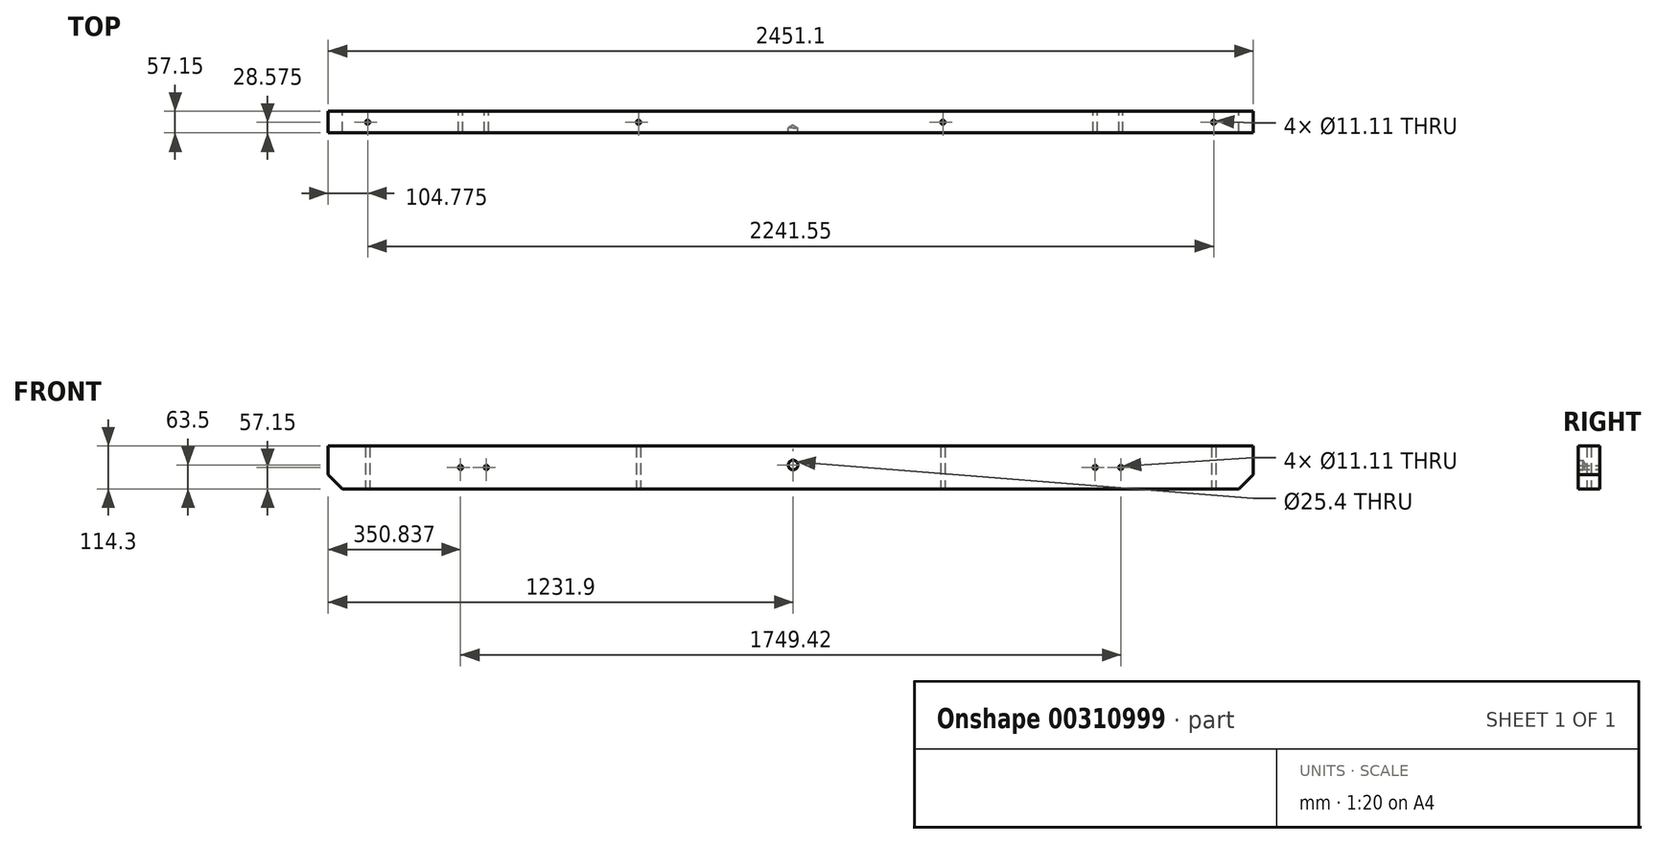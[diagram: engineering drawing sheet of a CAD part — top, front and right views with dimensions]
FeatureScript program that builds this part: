
annotation { "Feature Type Name" : "Feature", "Feature Type Description" : "" }
export const myFeature = defineFeature(function(context is Context, id is Id, definition is map)
    precondition{}
    {
        {
            var Q0;
            Q0=qCreatedBy(makeId("Front.planeOp"),FACE);
            var sketch = newSketch(context, id + "F0", { "sketchPlane" : qUnion([Q0])});
            skLineSegment(sketch, "E0", {"start": v(0, 0) * mm, "end": v(2451.1, 0) * mm});
            skLineSegment(sketch, "E1", {"start": v(2451.1, 0) * mm, "end": v(2451.1, -76.2) * mm});
            skLineSegment(sketch, "E2", {"start": v(0, 0) * mm, "end": v(0, -76.2) * mm});
            skLineSegment(sketch, "E3", {"start": v(0, -76.2) * mm, "end": v(38.1, -114.3) * mm});
            skLineSegment(sketch, "E4", {"start": v(2413, -114.3) * mm, "end": v(2451.1, -76.2) * mm});
            skLineSegment(sketch, "E5", {"start": v(38.1, -114.3) * mm, "end": v(2413, -114.3) * mm});
            skSolve(sketch);
        }
        {
            var Q0;
            Q0=makeQuery(id+"F0.imprint","IMPRINT",FACE,{"disambiguationData":[TD([[makeQuery(id+"F0.imprint","IMPRINT",EDGE,{"derivedFrom":sQuery(id+"F0.wireOp",EDGE,"E0")}),-1.0]])]});
            extrude(context, id + "F1", {"entities" : qUnion([Q0]), "depth" : 57.15 * mm});
        }
        {
            var Q0;
            Q0=makeQuery(id+"F1.opExtrude","SWEPT_FACE",FACE,{"disambiguationData":[OSD([sQuery(id+"F0.wireOp",EDGE,"E0")])]});
            var sketch = newSketch(context, id + "F2", { "sketchPlane" : qUnion([Q0])});
            skLineSegment(sketch, "E6", {"start": v(2451.1, -28.57) * mm, "end": v(0, -28.58) * mm, "construction": true});
            skLineSegment(sketch, "E7", {"start": v(104.78, 0) * mm, "end": v(104.78, -57.15) * mm, "construction": true});
            skLineSegment(sketch, "E8", {"start": v(822.33, 0) * mm, "end": v(822.33, -57.15) * mm, "construction": true});
            skLineSegment(sketch, "E9", {"start": v(2346.33, 0) * mm, "end": v(2346.33, -57.15) * mm, "construction": true});
            skLineSegment(sketch, "E10", {"start": v(1628.78, 0) * mm, "end": v(1628.78, -57.15) * mm, "construction": true});
            skPoint(sketch, "E11", {"position": v(2346.33, -28.57) * mm});
            skPoint(sketch, "E12", {"position": v(1628.78, -28.57) * mm});
            skPoint(sketch, "E13", {"position": v(822.33, -28.58) * mm});
            skPoint(sketch, "E14", {"position": v(104.78, -28.58) * mm});
            skSolve(sketch);
        }
        {
            var Q0;
            Q0=sQuery(id+"F2.wireOp",VERTEX,"E14");
            var Q1;
            Q1=sQuery(id+"F2.wireOp",VERTEX,"E13");
            var Q2;
            Q2=sQuery(id+"F2.wireOp",VERTEX,"E12");
            var Q3;
            Q3=sQuery(id+"F2.wireOp",VERTEX,"E11");
            var Q4;
            Q4=makeQuery(id+"F1.opExtrude","SWEPT_BODY",BODY,{"disambiguationData":[OSD([sQuery(id+"F0.wireOp",EDGE,"E0"),sQuery(id+"F0.wireOp",EDGE,"E1"),sQuery(id+"F0.wireOp",EDGE,"E2"),sQuery(id+"F0.wireOp",EDGE,"E3"),sQuery(id+"F0.wireOp",EDGE,"E4"),sQuery(id+"F0.wireOp",EDGE,"E5")])]});
            hole(context, id + "F3", {"style" : HoleStyle.SIMPLE, "endStyle" : HoleEndStyle.THROUGH, "holeDiameter" : 11.1 * mm, "tappedDepth" : 12.7 * mm, "tapClearance" : 3, "locations" : qUnion([Q0, Q1, Q2, Q3]), "scope" : qUnion([Q4])});
        }
        {
            var Q0;
            Q0=makeQuery(id+"F1.opExtrude","CAP_FACE",FACE,{"disambiguationData":[OSD([sQuery(id+"F0.wireOp",EDGE,"E0"),sQuery(id+"F0.wireOp",EDGE,"E1"),sQuery(id+"F0.wireOp",EDGE,"E2"),sQuery(id+"F0.wireOp",EDGE,"E3"),sQuery(id+"F0.wireOp",EDGE,"E4"),sQuery(id+"F0.wireOp",EDGE,"E5")])],"isStart":false});
            var sketch = newSketch(context, id + "F4", { "sketchPlane" : qUnion([Q0])});
            skLineSegment(sketch, "E15", {"start": v(0, -57.15) * mm, "end": v(2451.1, -57.15) * mm, "construction": true});
            skPoint(sketch, "E16", {"position": v(350.84, -57.15) * mm});
            skPoint(sketch, "E17", {"position": v(419.1, -57.15) * mm});
            skPoint(sketch, "E18", {"position": v(2100.26, -57.15) * mm});
            skPoint(sketch, "E19", {"position": v(2032, -57.15) * mm});
            skSolve(sketch);
        }
        {
            var Q0;
            Q0=sQuery(id+"F4.wireOp",VERTEX,"E16");
            var Q1;
            Q1=sQuery(id+"F4.wireOp",VERTEX,"E17");
            var Q2;
            Q2=sQuery(id+"F4.wireOp",VERTEX,"E19");
            var Q3;
            Q3=sQuery(id+"F4.wireOp",VERTEX,"E18");
            var Q4;
            Q4=makeQuery(id+"F1.opExtrude","SWEPT_BODY",BODY,{"disambiguationData":[OSD([sQuery(id+"F0.wireOp",EDGE,"E0"),sQuery(id+"F0.wireOp",EDGE,"E1"),sQuery(id+"F0.wireOp",EDGE,"E2"),sQuery(id+"F0.wireOp",EDGE,"E3"),sQuery(id+"F0.wireOp",EDGE,"E4"),sQuery(id+"F0.wireOp",EDGE,"E5")])]});
            hole(context, id + "F5", {"style" : HoleStyle.SIMPLE, "endStyle" : HoleEndStyle.THROUGH, "holeDiameter" : 11.1 * mm, "tappedDepth" : 12.7 * mm, "tapClearance" : 3, "locations" : qUnion([Q0, Q1, Q2, Q3]), "scope" : qUnion([Q4])});
        }
        {
            var Q0;
            Q0=makeQuery(id+"F1.opExtrude","CAP_FACE",FACE,{"disambiguationData":[OSD([sQuery(id+"F0.wireOp",EDGE,"E0"),sQuery(id+"F0.wireOp",EDGE,"E1"),sQuery(id+"F0.wireOp",EDGE,"E2"),sQuery(id+"F0.wireOp",EDGE,"E3"),sQuery(id+"F0.wireOp",EDGE,"E4"),sQuery(id+"F0.wireOp",EDGE,"E5")])],"isStart":false});
            var sketch = newSketch(context, id + "F6", { "sketchPlane" : qUnion([Q0])});
            skPoint(sketch, "E20", {"position": v(1231.9, -50.8) * mm});
            skSolve(sketch);
        }
        {
            var Q0;
            Q0=sQuery(id+"F6.wireOp",VERTEX,"E20");
            var Q1;
            Q1=makeQuery(id+"F1.opExtrude","SWEPT_BODY",BODY,{"disambiguationData":[OSD([sQuery(id+"F0.wireOp",EDGE,"E0"),sQuery(id+"F0.wireOp",EDGE,"E1"),sQuery(id+"F0.wireOp",EDGE,"E2"),sQuery(id+"F0.wireOp",EDGE,"E3"),sQuery(id+"F0.wireOp",EDGE,"E4"),sQuery(id+"F0.wireOp",EDGE,"E5")])]});
            hole(context, id + "F7", {"style" : HoleStyle.SIMPLE, "endStyle" : HoleEndStyle.BLIND, "holeDiameter" : 25.4 * mm, "holeDepth" : 12.7 * mm, "tappedDepth" : 12.7 * mm, "tapClearance" : 3, "locations" : qUnion([Q0]), "scope" : qUnion([Q1])});
        }
    });
